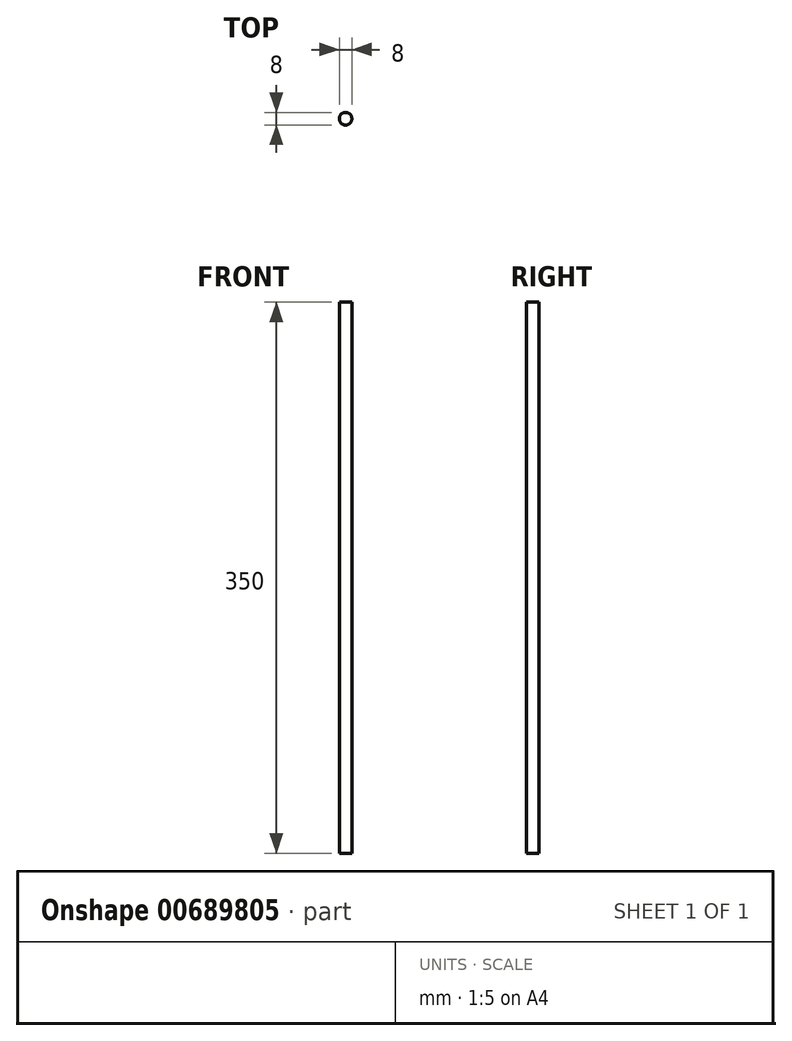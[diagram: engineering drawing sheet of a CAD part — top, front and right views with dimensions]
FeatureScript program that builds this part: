
annotation { "Feature Type Name" : "Feature", "Feature Type Description" : "" }
export const myFeature = defineFeature(function(context is Context, id is Id, definition is map)
    precondition{}
    {
        {
            var Q0;
            Q0=qCreatedBy(makeId("Top.planeOp"),FACE);
            var sketch = newSketch(context, id + "F0", { "sketchPlane" : qUnion([Q0])});
            skCircle(sketch, "E0", {"center": v(0, 0) * mm, "radius": 4 * mm});
            skSolve(sketch);
        }
        {
            var Q0;
            Q0=makeQuery(id+"F0.imprint","IMPRINT",FACE,{"disambiguationData":[TD([[makeQuery(id+"F0.imprint","IMPRINT",EDGE,{"derivedFrom":sQuery(id+"F0.wireOp",EDGE,"E0")}),1.0]])]});
            extrude(context, id + "F1", {"entities" : qUnion([Q0]), "depth" : 350 * mm, "offsetDistance" : 25 * mm});
        }
    });
